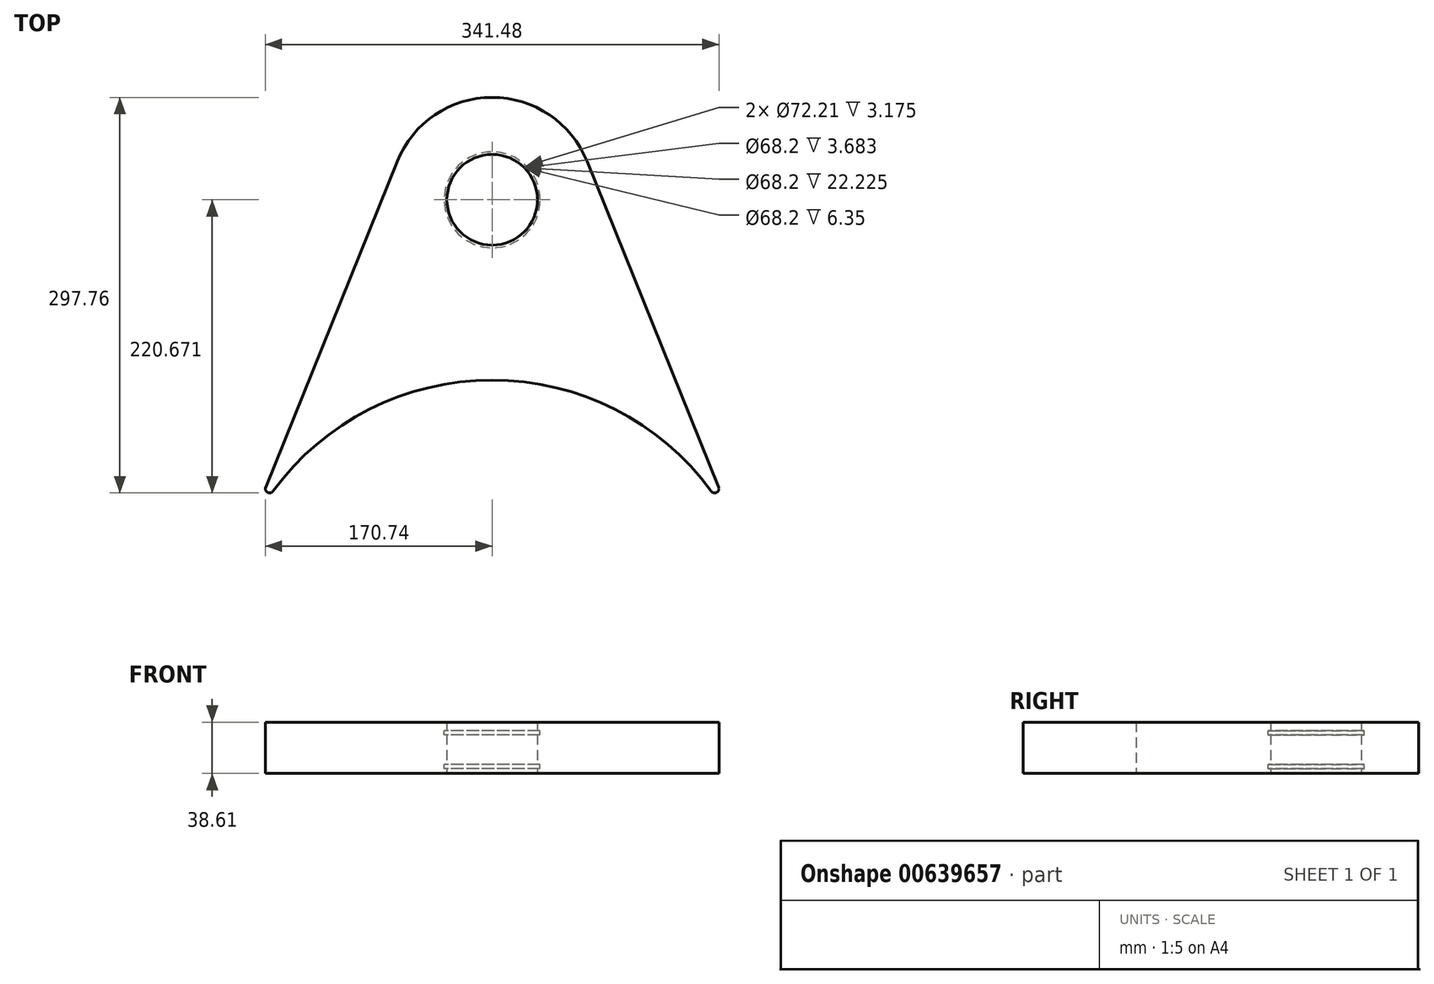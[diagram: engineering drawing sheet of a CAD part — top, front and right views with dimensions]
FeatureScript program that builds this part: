
annotation { "Feature Type Name" : "Feature", "Feature Type Description" : "" }
export const myFeature = defineFeature(function(context is Context, id is Id, definition is map)
    precondition{}
    {
        {
            var Q0;
            Q0=qCreatedBy(makeId("Top.planeOp"),FACE);
            var sketch = newSketch(context, id + "F0", { "sketchPlane" : qUnion([Q0])});
            skArc(sketch, "E0", {"start": v(165, 120.76) * mm, "mid": v(0, 204.47) * mm, "end": v(-165, 120.76) * mm});
            skLineSegment(sketch, "E1", {"start": v(0, 0) * mm, "end": v(0, 340.13) * mm, "construction": true});
            skCircle(sketch, "E2", {"center": v(0, 340.13) * mm, "radius": 34.1 * mm});
            skArc(sketch, "E3", {"start": v(71.48, 369) * mm, "mid": v(0, 417.22) * mm, "end": v(-71.48, 369) * mm});
            skLineSegment(sketch, "E4", {"start": v(-71.48, 369) * mm, "end": v(-170.5, 123.83) * mm});
            skLineSegment(sketch, "E5.MirrorCS", {"start": v(71.48, 369) * mm, "end": v(170.5, 123.83) * mm});
            skPoint(sketch, "E6.visualSharp", {"position": v(-189.59, 76.58) * mm});
            skArc(sketch, "E6.filletArc", {"start": v(-170.5, 123.83) * mm, "mid": v(-169.1, 119.86) * mm, "end": v(-165, 120.76) * mm});
            skPoint(sketch, "E7.visualSharp", {"position": v(189.59, 76.58) * mm});
            skArc(sketch, "E7.filletArc", {"start": v(165, 120.76) * mm, "mid": v(169.1, 119.86) * mm, "end": v(170.5, 123.83) * mm});
            skSolve(sketch);
        }
        {
            var Q0;
            Q0 = qSketchRegion(id + "F0", true);
            extrude(context, id + "F1", {"entities" : qUnion([Q0]), "depth" : 38.6 * mm, "offsetDistance" : 25.4 * mm});
        }
        {
            var Q0;
            Q0=makeQuery(id+"F1.opExtrude","CAP_FACE",FACE,{"disambiguationData":[OSD([sQuery(id+"F0.wireOp",EDGE,"E0"),sQuery(id+"F0.wireOp",EDGE,"E2"),sQuery(id+"F0.wireOp",EDGE,"E3"),sQuery(id+"F0.wireOp",EDGE,"E4"),sQuery(id+"F0.wireOp",EDGE,"E5.MirrorCS"),sQuery(id+"F0.wireOp",EDGE,"E6.filletArc"),sQuery(id+"F0.wireOp",EDGE,"E7.filletArc")])],"isStart":false});
            cPlane(context, id + "F2", {"entities" : qUnion([Q0]), "cplaneType" : CPlaneType.OFFSET, "offset" : 6.35 * mm, "oppositeDirection" : true, "width" : 152.4 * mm, "height" : 152.4 * mm});
        }
        {
            var Q0;
            Q0=qCreatedBy(id+"F2.planeOp",FACE);
            var sketch = newSketch(context, id + "F3", { "sketchPlane" : qUnion([Q0])});
            skCircle(sketch, "E8.0", {"center": v(0, 340.13) * mm, "radius": 34.1 * mm, "construction": true});
            skCircle(sketch, "E9", {"center": v(0, 340.13) * mm, "radius": 36.1 * mm});
            skSolve(sketch);
        }
        {
            var Q0;
            Q0 = qSketchRegion(id + "F3", true);
            extrude(context, id + "F4", {"entities" : qUnion([Q0]), "operationType" : NewBodyOperationType.REMOVE, "oppositeDirection" : true, "depth" : 3.17 * mm, "offsetDistance" : 25.4 * mm});
        }
        {
            var Q0;
            Q0=makeQuery(id+"F1.opExtrude","CAP_FACE",FACE,{"disambiguationData":[OSD([sQuery(id+"F0.wireOp",EDGE,"E0"),sQuery(id+"F0.wireOp",EDGE,"E2"),sQuery(id+"F0.wireOp",EDGE,"E3"),sQuery(id+"F0.wireOp",EDGE,"E4"),sQuery(id+"F0.wireOp",EDGE,"E5.MirrorCS"),sQuery(id+"F0.wireOp",EDGE,"E6.filletArc"),sQuery(id+"F0.wireOp",EDGE,"E7.filletArc")])],"isStart":false});
            cPlane(context, id + "F5", {"entities" : qUnion([Q0]), "cplaneType" : CPlaneType.OFFSET, "offset" : 31.75 * mm, "oppositeDirection" : true, "width" : 152.4 * mm, "height" : 152.4 * mm});
        }
        {
            var Q0;
            Q0=qCreatedBy(id+"F5.planeOp",FACE);
            var sketch = newSketch(context, id + "F6", { "sketchPlane" : qUnion([Q0])});
            skCircle(sketch, "E10.0", {"center": v(0, 340.13) * mm, "radius": 34.1 * mm, "construction": true});
            skCircle(sketch, "E11", {"center": v(0, 340.13) * mm, "radius": 36.1 * mm});
            skSolve(sketch);
        }
        {
            var Q0;
            Q0 = qSketchRegion(id + "F6", true);
            extrude(context, id + "F7", {"entities" : qUnion([Q0]), "operationType" : NewBodyOperationType.REMOVE, "oppositeDirection" : true, "depth" : 3.17 * mm, "offsetDistance" : 25.4 * mm});
        }
    });
